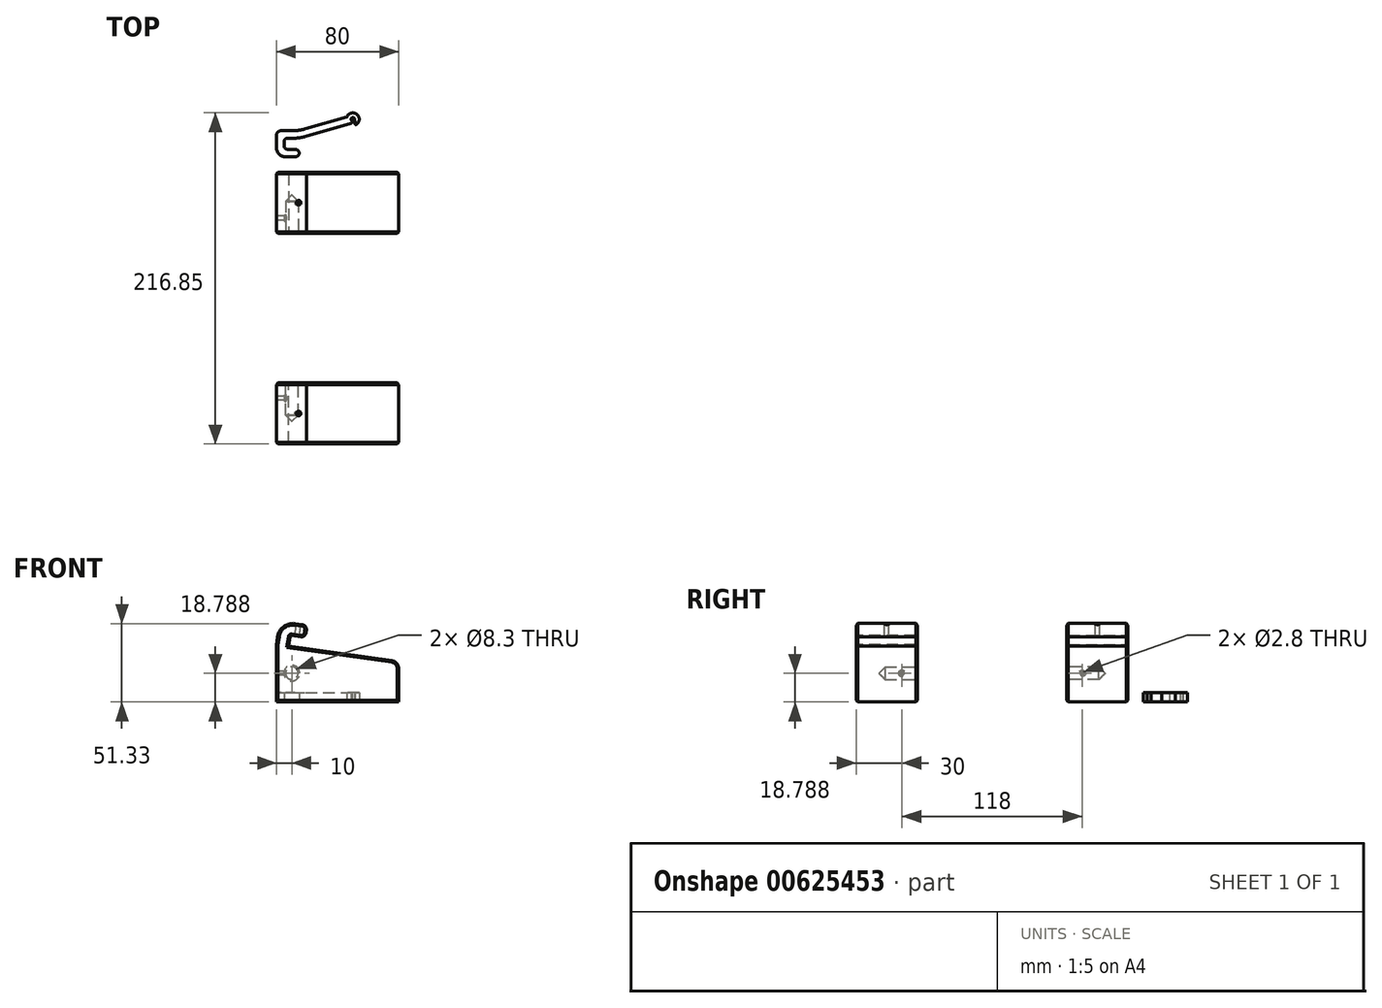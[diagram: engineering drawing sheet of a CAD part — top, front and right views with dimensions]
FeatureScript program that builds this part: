
annotation { "Feature Type Name" : "Feature", "Feature Type Description" : "" }
export const myFeature = defineFeature(function(context is Context, id is Id, definition is map)
    precondition{}
    {
        {
            var Q0;
            Q0=qCreatedBy(makeId("Front.planeOp"),FACE);
            var sketch = newSketch(context, id + "F0", { "sketchPlane" : qUnion([Q0])});
            skLineSegment(sketch, "E0", {"start": v(0, 0) * mm, "end": v(267.37, 0) * mm});
            skLineSegment(sketch, "E1", {"start": v(267.37, 0) * mm, "end": v(0, 37.58) * mm});
            skLineSegment(sketch, "E2", {"start": v(0, 37.58) * mm, "end": v(0, 0) * mm});
            skLineSegment(sketch, "E3", {"start": v(80, 26.33) * mm, "end": v(80, 0) * mm});
            skSolve(sketch);
        }
        {
            var Q0;
            {var subQ0=sQuery(id+"F0.wireOp",EDGE,"E2");Q0=makeQuery(id+"F0.imprint","IMPRINT",FACE,{"disambiguationData":[TD([[makeQuery(id+"F0.imprint","IMPRINT",EDGE,{"derivedFrom":subQ0}),1.0]])]});}
            extrude(context, id + "F1", {"entities" : qUnion([Q0]), "depth" : 40 * mm, "offsetDistance" : 25 * mm});
        }
        {
            var Q0;
            Q0=makeQuery(id+"F1.opExtrude","CAP_FACE",FACE,{"disambiguationData":[OSD([sQuery(id+"F0.wireOp",EDGE,"E0"),sQuery(id+"F0.wireOp",EDGE,"E1"),sQuery(id+"F0.wireOp",EDGE,"E2"),sQuery(id+"F0.wireOp",EDGE,"E3")])],"isStart":false});
            var sketch = newSketch(context, id + "F2", { "sketchPlane" : qUnion([Q0])});
            skCircle(sketch, "E4", {"center": v(10, 18.79) * mm, "radius": 4.15 * mm});
            skPoint(sketch, "E4.centerSnap0", {"position": v(0, 18.79) * mm});
            skSolve(sketch);
        }
        {
            var Q0;
            Q0=makeQuery(id+"F2.imprint","IMPRINT",FACE,{"disambiguationData":[TD([[makeQuery(id+"F2.imprint","IMPRINT",EDGE,{"derivedFrom":sQuery(id+"F2.wireOp",EDGE,"E4")}),1.0]])]});
            extrude(context, id + "F3", {"entities" : qUnion([Q0]), "operationType" : NewBodyOperationType.REMOVE, "oppositeDirection" : true, "depth" : 25 * mm, "offsetDistance" : 25 * mm});
        }
        {
            var Q0;
            Q0=makeQuery(id+"F3.boolean.opBoolean","COPY",EDGE,{"derivedFrom":makeQuery(id+"F3.opExtrude","CAP_EDGE",EDGE,{"disambiguationData":[OSD([sQuery(id+"F2.wireOp",EDGE,"E4")])],"isStart":false})});
            chamfer(context, id + "F4", {"entities" : qUnion([Q0]), "width" : 4 * mm, "tangentPropagation" : true});
        }
        {
            var Q0;
            Q0=makeQuery(id+"F1.opExtrude","SWEPT_FACE",FACE,{"disambiguationData":[OSD([sQuery(id+"F0.wireOp",EDGE,"E2")])]});
            var sketch = newSketch(context, id + "F5", { "sketchPlane" : qUnion([Q0])});
            skCircle(sketch, "E5", {"center": v(30, 18.79) * mm, "radius": 1.4 * mm});
            skPoint(sketch, "E5.centerSnap0", {"position": v(40, 18.79) * mm});
            skSolve(sketch);
        }
        {
            var Q0;
            Q0=makeQuery(id+"F5.imprint","IMPRINT",FACE,{"disambiguationData":[TD([[makeQuery(id+"F5.imprint","IMPRINT",EDGE,{"derivedFrom":sQuery(id+"F5.wireOp",EDGE,"E5")}),1.0]])]});
            extrude(context, id + "F6", {"entities" : qUnion([Q0]), "operationType" : NewBodyOperationType.REMOVE, "oppositeDirection" : true, "depth" : 10 * mm, "offsetDistance" : 25 * mm});
        }
        {
            var Q0;
            Q0=makeQuery(id+"F1.opExtrude","CAP_FACE",FACE,{"disambiguationData":[OSD([sQuery(id+"F0.wireOp",EDGE,"E0"),sQuery(id+"F0.wireOp",EDGE,"E1"),sQuery(id+"F0.wireOp",EDGE,"E2"),sQuery(id+"F0.wireOp",EDGE,"E3")])],"isStart":false});
            var sketch = newSketch(context, id + "F7", { "sketchPlane" : qUnion([Q0])});
            skLineSegment(sketch, "E6", {"start": v(0, 37.58) * mm, "end": v(0.72, 42.73) * mm});
            skLineSegment(sketch, "E7", {"start": v(12.02, 51.24) * mm, "end": v(19.94, 50.12) * mm});
            skLineSegment(sketch, "E8", {"start": v(19.94, 50.12) * mm, "end": v(18.83, 42.2) * mm});
            skLineSegment(sketch, "E9", {"start": v(18.83, 42.2) * mm, "end": v(8.92, 43.6) * mm});
            skLineSegment(sketch, "E10", {"start": v(8.92, 43.6) * mm, "end": v(7.92, 36.46) * mm});
            skPoint(sketch, "E11.visualSharp", {"position": v(2.12, 52.63) * mm});
            skArc(sketch, "E11.filletArc", {"start": v(12.02, 51.24) * mm, "mid": v(4.6, 49.32) * mm, "end": v(0.72, 42.73) * mm});
            skSolve(sketch);
        }
        {
            var Q0;
            {var subQ0=sQuery(id+"F7.wireOp",EDGE,"E6");Q0=makeQuery(id+"F7.imprint","IMPRINT",FACE,{"disambiguationData":[TD([[makeQuery(id+"F7.imprint","IMPRINT",EDGE,{"derivedFrom":subQ0}),-1.0]])]});}
            var Q1;
            Q1=makeQuery(id+"F1.opExtrude","CAP_FACE",FACE,{"disambiguationData":[OSD([sQuery(id+"F0.wireOp",EDGE,"E0"),sQuery(id+"F0.wireOp",EDGE,"E1"),sQuery(id+"F0.wireOp",EDGE,"E2"),sQuery(id+"F0.wireOp",EDGE,"E3")])],"isStart":true});
            extrude(context, id + "F8", {"entities" : qUnion([Q0]), "operationType" : NewBodyOperationType.ADD, "endBound" : BoundingType.UP_TO_SURFACE, "oppositeDirection" : true, "depth" : 25 * mm, "endBoundEntityFace" : qUnion([Q1]), "offsetDistance" : 25 * mm});
        }
        {
            var Q0;
            Q0=makeQuery(id+"F8.opExtrude","SWEPT_EDGE",EDGE,{"disambiguationData":[OSD([sQuery(id+"F7.wireOp",EDGE,"E9"),sQuery(id+"F7.wireOp",EDGE,"E10")])]});
            var Q1;
            Q1=makeQuery(id+"F8.opExtrude","SWEPT_EDGE",EDGE,{"disambiguationData":[OSD([sQuery(id+"F0.wireOp",EDGE,"E1"),sQuery(id+"F7.wireOp",EDGE,"E10")])]});
            fillet(context, id + "F9", {"entities" : qUnion([Q0, Q1]), "radius" : 1 * mm, "tangentPropagation" : true, "allowEdgeOverflow" : false});
        }
        {
            var Q0;
            Q0=makeQuery(id+"F8.opExtrude","SWEPT_EDGE",EDGE,{"disambiguationData":[OSD([sQuery(id+"F7.wireOp",EDGE,"E7"),sQuery(id+"F7.wireOp",EDGE,"E8")])]});
            var Q1;
            Q1=makeQuery(id+"F8.opExtrude","SWEPT_EDGE",EDGE,{"disambiguationData":[OSD([sQuery(id+"F7.wireOp",EDGE,"E8"),sQuery(id+"F7.wireOp",EDGE,"E9")])]});
            fillet(context, id + "F10", {"entities" : qUnion([Q0, Q1]), "radius" : 3 * mm, "tangentPropagation" : true, "allowEdgeOverflow" : false});
        }
        {
            var Q0;
            Q0=makeQuery(id+"F1.opExtrude","SWEPT_EDGE",EDGE,{"disambiguationData":[OSD([sQuery(id+"F0.wireOp",EDGE,"E1"),sQuery(id+"F0.wireOp",EDGE,"E3")])]});
            fillet(context, id + "F11", {"entities" : qUnion([Q0]), "radius" : 5 * mm, "tangentPropagation" : true, "allowEdgeOverflow" : false});
        }
        {
            var Q0;
            Q0=makeQuery(id+"F3.boolean.opBoolean","COPY",EDGE,{"derivedFrom":makeQuery(id+"F3.opExtrude","CAP_EDGE",EDGE,{"disambiguationData":[OSD([sQuery(id+"F2.wireOp",EDGE,"E4")])],"isStart":true})});
            var Q1;
            Q1=makeQuery(id+"F6.boolean.opBoolean","COPY",EDGE,{"derivedFrom":makeQuery(id+"F6.opExtrude","CAP_EDGE",EDGE,{"disambiguationData":[OSD([sQuery(id+"F5.wireOp",EDGE,"E5")])],"isStart":true})});
            var Q2;
            Q2=makeQuery(id+"F6.boolean.opBoolean","INTERSECT",EDGE,{"derivedFrom":[makeQuery(id+"F3.boolean.opBoolean","COPY",FACE,{"derivedFrom":makeQuery(id+"F3.opExtrude","SWEPT_FACE",FACE,{"disambiguationData":[OSD([sQuery(id+"F2.wireOp",EDGE,"E4")])]})}),makeQuery(id+"F6.opExtrude","SWEPT_FACE",FACE,{"disambiguationData":[OSD([sQuery(id+"F5.wireOp",EDGE,"E5")])]})]});
            chamfer(context, id + "F12", {"entities" : qUnion([Q0, Q1, Q2]), "width" : 1 * mm, "tangentPropagation" : true});
        }
        {
            var Q0;
            {var subQ0=sQuery(id+"F0.wireOp",EDGE,"E1");Q0=makeQuery(id+"F8.boolean.opBoolean","MERGE",FACE,{"derivedFrom":[makeQuery(id+"F1.opExtrude","CAP_FACE",FACE,{"disambiguationData":[OSD([sQuery(id+"F0.wireOp",EDGE,"E0"),subQ0,sQuery(id+"F0.wireOp",EDGE,"E2"),sQuery(id+"F0.wireOp",EDGE,"E3")])],"isStart":false}),makeQuery(id+"F8.opExtrude","CAP_FACE",FACE,{"disambiguationData":[OSD([subQ0,sQuery(id+"F7.wireOp",EDGE,"E6"),sQuery(id+"F7.wireOp",EDGE,"E7"),sQuery(id+"F7.wireOp",EDGE,"E8"),sQuery(id+"F7.wireOp",EDGE,"E9"),sQuery(id+"F7.wireOp",EDGE,"E10"),sQuery(id+"F7.wireOp",EDGE,"E11.filletArc")])],"isStart":true})]});}
            var Q1;
            {var subQ0=sQuery(id+"F0.wireOp",EDGE,"E3");var subQ1=sQuery(id+"F0.wireOp",EDGE,"E2");var subQ2=sQuery(id+"F0.wireOp",EDGE,"E1");var subQ3=sQuery(id+"F0.wireOp",EDGE,"E0");Q1=makeQuery(id+"F8.boolean.opBoolean","MERGE",FACE,{"derivedFrom":[makeQuery(id+"F1.opExtrude","CAP_FACE",FACE,{"disambiguationData":[OSD([subQ3,subQ2,subQ1,subQ0])],"isStart":true}),makeQuery(id+"F8.opExtrude","CAP_FACE",FACE,{"disambiguationData":[OSD([subQ3,subQ2,subQ1,subQ0])],"isStart":false})]});}
            chamfer(context, id + "F13", {"entities" : qUnion([Q0, Q1]), "width" : 1 * mm, "tangentPropagation" : true});
        }
        {
            var Q0;
            Q0=makeQuery(id+"F8.opExtrude","SWEPT_FACE",FACE,{"disambiguationData":[OSD([sQuery(id+"F7.wireOp",EDGE,"E7")])]});
            var sketch = newSketch(context, id + "F14", { "sketchPlane" : qUnion([Q0])});
            skCircle(sketch, "E12", {"center": v(7.27, -20) * mm, "radius": 1.5 * mm});
            skPoint(sketch, "E12.centerSnap0", {"position": v(7.27, -39) * mm});
            skPoint(sketch, "E12.centerSnap1", {"position": v(9.77, -20) * mm});
            skSolve(sketch);
        }
        {
            var Q0;
            Q0=makeQuery(id+"F14.imprint","IMPRINT",FACE,{"disambiguationData":[TD([[makeQuery(id+"F14.imprint","IMPRINT",EDGE,{"derivedFrom":sQuery(id+"F14.wireOp",EDGE,"E12")}),1.0]])]});
            extrude(context, id + "F15", {"entities" : qUnion([Q0]), "operationType" : NewBodyOperationType.REMOVE, "oppositeDirection" : true, "depth" : 10 * mm, "offsetDistance" : 25 * mm});
        }
        {
            var Q0;
            Q0=makeQuery(id+"F1.opExtrude","SWEPT_BODY",BODY,{"disambiguationData":[OSD([sQuery(id+"F0.wireOp",EDGE,"E0"),sQuery(id+"F0.wireOp",EDGE,"E1"),sQuery(id+"F0.wireOp",EDGE,"E2"),sQuery(id+"F0.wireOp",EDGE,"E3")])]});
            var Q1;
            Q1=qCreatedBy(makeId("Top.planeOp"),FACE);
            mirror(context, id + "F16", {"entities" : qUnion([Q0]), "mirrorPlane" : qUnion([Q1])});
        }
        {
            var Q0;
            Q0=makeQuery(id+"F16.opPattern","COPY",BODY,{"derivedFrom":makeQuery(id+"F1.opExtrude","SWEPT_BODY",BODY,{"disambiguationData":[OSD([sQuery(id+"F0.wireOp",EDGE,"E0"),sQuery(id+"F0.wireOp",EDGE,"E1"),sQuery(id+"F0.wireOp",EDGE,"E2"),sQuery(id+"F0.wireOp",EDGE,"E3")])]}),"instanceName":"1"});
            transform(context, id + "F17", {"entities" : qUnion([Q0]), "transformType" : TransformType.TRANSLATION_3D, "dx" : 0 * mm, "dy" : 0 * mm, "dz" : -2 * mm, "makeCopy" : false});
        }
        {
            var Q0;
            Q0=makeQuery(id+"F16.opPattern","COPY",BODY,{"derivedFrom":makeQuery(id+"F1.opExtrude","SWEPT_BODY",BODY,{"disambiguationData":[OSD([sQuery(id+"F0.wireOp",EDGE,"E0"),sQuery(id+"F0.wireOp",EDGE,"E1"),sQuery(id+"F0.wireOp",EDGE,"E2"),sQuery(id+"F0.wireOp",EDGE,"E3")])]}),"instanceName":"1"});
            var Q1;
            {var subQ0=sQuery(id+"F0.wireOp",EDGE,"E0");Q1=makeQuery(id+"F13.opChamfer","BLEND_EDGE",EDGE,{"blendedFrom":[makeQuery(id+"F1.opExtrude","CAP_EDGE",EDGE,{"disambiguationData":[OSD([subQ0])],"isStart":false}),makeQuery(id+"F1.opExtrude","SWEPT_FACE",FACE,{"disambiguationData":[OSD([subQ0])]})],"blendedInto":[makeQuery(id+"F1.opExtrude","SWEPT_FACE",FACE,{"disambiguationData":[OSD([subQ0])]})]});}
            transform(context, id + "F18", {"entities" : qUnion([Q0]), "transformType" : TransformType.ROTATION, "transformAxis" : qUnion([Q1]), "angle" : 180 * degree, "makeCopy" : false});
        }
        {
            var Q0;
            Q0=makeQuery(id+"F16.opPattern","COPY",BODY,{"derivedFrom":makeQuery(id+"F1.opExtrude","SWEPT_BODY",BODY,{"disambiguationData":[OSD([sQuery(id+"F0.wireOp",EDGE,"E0"),sQuery(id+"F0.wireOp",EDGE,"E1"),sQuery(id+"F0.wireOp",EDGE,"E2"),sQuery(id+"F0.wireOp",EDGE,"E3")])]}),"instanceName":"1"});
            transform(context, id + "F19", {"entities" : qUnion([Q0]), "transformType" : TransformType.TRANSLATION_3D, "dx" : 0 * mm, "dy" : -100 * mm, "dz" : -2 * mm, "makeCopy" : false});
        }
        {
            var Q0;
            Q0=qCreatedBy(makeId("Top.planeOp"),FACE);
            var sketch = newSketch(context, id + "F20", { "sketchPlane" : qUnion([Q0])});
            skLineSegment(sketch, "E13", {"start": v(0, 10) * mm, "end": v(0, 27.2) * mm});
            skLineSegment(sketch, "E14", {"start": v(0, 27.2) * mm, "end": v(15, 27.2) * mm});
            skLineSegment(sketch, "E15", {"start": v(50, 22.2) * mm, "end": v(5, 22.2) * mm});
            skLineSegment(sketch, "E16", {"start": v(5, 22.2) * mm, "end": v(5, 15) * mm});
            skLineSegment(sketch, "E17", {"start": v(5, 15) * mm, "end": v(15, 15) * mm});
            skLineSegment(sketch, "E18", {"start": v(15, 15) * mm, "end": v(15, 10) * mm});
            skLineSegment(sketch, "E19", {"start": v(15, 10) * mm, "end": v(0, 10) * mm});
            skPoint(sketch, "E20", {"position": v(50, 34.7) * mm});
            skCircle(sketch, "E21", {"center": v(50, 34.7) * mm, "radius": 1.15 * mm});
            skLineSegment(sketch, "E22", {"start": v(15, 22.2) * mm, "end": v(15, 27.2) * mm});
            skCircle(sketch, "E23", {"center": v(50, 34.7) * mm, "radius": 2.5 * mm});
            skLineSegment(sketch, "E24", {"start": v(49.3, 33.78) * mm, "end": v(49.7, 32.22) * mm});
            skLineSegment(sketch, "E25", {"start": v(49.3, 33.78) * mm, "end": v(51.05, 34.23) * mm});
            skLineSegment(sketch, "E26", {"start": v(51.05, 34.23) * mm, "end": v(51.45, 32.66) * mm});
            skLineSegment(sketch, "E27", {"start": v(15, 22.2) * mm, "end": v(49.7, 32.22) * mm});
            skLineSegment(sketch, "E28", {"start": v(15, 27.2) * mm, "end": v(49.3, 37.1) * mm});
            skCircle(sketch, "E29", {"center": v(50, 34.7) * mm, "radius": 4.15 * mm});
            skLineSegment(sketch, "E30", {"start": v(51.45, 32.66) * mm, "end": v(51.29, 30.76) * mm});
            skSolve(sketch);
        }
        {
            var Q0;
            Q0=makeQuery(id+"F20.imprint","IMPRINT",FACE,{"disambiguationData":[TD([[makeQuery(id+"F20.imprint","IMPRINT",EDGE,{"derivedFrom":sQuery(id+"F20.wireOp",EDGE,"E13")}),-1.0]])]});
            var Q1;
            Q1=makeQuery(id+"F20.imprint","IMPRINT",FACE,{"disambiguationData":[TD([[makeQuery(id+"F20.imprint","IMPRINT",EDGE,{"derivedFrom":sQuery(id+"F20.wireOp",EDGE,"E22")}),-1.0]])]});
            var Q2;
            {var subQ3=sQuery(id+"F20.wireOp",EDGE,"E24");Q2=makeQuery(id+"F20.imprint","IMPRINT",FACE,{"disambiguationData":[TD([[makeQuery(id+"F20.imprint","IMPRINT",EDGE,{"derivedFrom":subQ3}),-1.0]])]});}
            var Q3;
            {var subQ1=sQuery(id+"F20.wireOp",EDGE,"E23");var subQ3=sQuery(id+"F20.wireOp",EDGE,"E28");var subQ4=makeQuery(id+"F20.imprint","INTERSECT",VERTEX,{"derivedFrom":[subQ1,subQ3]});Q3=makeQuery(id+"F20.imprint","IMPRINT",FACE,{"disambiguationData":[TD([[makeQuery(id+"F20.imprint","IMPRINT",EDGE,{"disambiguationData":[TD([[subQ4,1.0]])],"derivedFrom":subQ3}),-1.0]])]});}
            var Q4;
            {var subQ1=sQuery(id+"F20.wireOp",EDGE,"E23");var subQ8=makeQuery(id+"F20.imprint","INTERSECT",VERTEX,{"derivedFrom":[subQ1,sQuery(id+"F20.wireOp",EDGE,"E26")]});Q4=makeQuery(id+"F20.imprint","IMPRINT",FACE,{"disambiguationData":[TD([[makeQuery(id+"F20.imprint","IMPRINT",EDGE,{"disambiguationData":[TD([[subQ8,-1.0]])],"derivedFrom":subQ1}),-1.0]])]});}
            extrude(context, id + "F21", {"entities" : qUnion([Q0, Q1, Q2, Q3, Q4]), "depth" : 6 * mm, "offsetDistance" : 25 * mm});
        }
        {
            var Q0;
            Q0=makeQuery(id+"F21.opExtrude","SWEPT_EDGE",EDGE,{"disambiguationData":[OSD([sQuery(id+"F20.wireOp",EDGE,"E16"),sQuery(id+"F20.wireOp",EDGE,"E17")])]});
            var Q1;
            Q1=makeQuery(id+"F21.opExtrude","SWEPT_EDGE",EDGE,{"disambiguationData":[OSD([sQuery(id+"F20.wireOp",EDGE,"E15"),sQuery(id+"F20.wireOp",EDGE,"E16")])]});
            fillet(context, id + "F22", {"entities" : qUnion([Q0, Q1]), "radius" : 2 * mm, "tangentPropagation" : true, "allowEdgeOverflow" : false});
        }
        {
            var Q0;
            Q0=makeQuery(id+"F21.opExtrude","SWEPT_EDGE",EDGE,{"disambiguationData":[OSD([sQuery(id+"F20.wireOp",EDGE,"E17"),sQuery(id+"F20.wireOp",EDGE,"E18")])]});
            var Q1;
            Q1=makeQuery(id+"F21.opExtrude","SWEPT_EDGE",EDGE,{"disambiguationData":[OSD([sQuery(id+"F20.wireOp",EDGE,"E18"),sQuery(id+"F20.wireOp",EDGE,"E19")])]});
            var Q2;
            Q2=makeQuery(id+"F21.opExtrude","SWEPT_EDGE",EDGE,{"disambiguationData":[OSD([sQuery(id+"F20.wireOp",EDGE,"E14"),sQuery(id+"F20.wireOp",EDGE,"1yIS3Pmy-LfiJ-1xFZ-S5RH-yLwdn8sh1kng")])]});
            var Q3;
            Q3=makeQuery(id+"F21.opExtrude","SWEPT_EDGE",EDGE,{"disambiguationData":[OSD([sQuery(id+"F20.wireOp",EDGE,"1yIS3Pmy-LfiJ-1xFZ-S5RH-yLwdn8sh1kng"),sQuery(id+"F20.wireOp",EDGE,"XR6DbFyx-l4WN-efZy-Vrzi-RNmAAhyDzetU")])]});
            fillet(context, id + "F23", {"entities" : qUnion([Q0, Q1, Q2, Q3]), "radius" : 3 * mm, "tangentPropagation" : true, "allowEdgeOverflow" : false});
        }
        {
            var Q0;
            Q0=makeQuery(id+"F21.opExtrude","SWEPT_EDGE",EDGE,{"disambiguationData":[OSD([sQuery(id+"F20.wireOp",EDGE,"E13"),sQuery(id+"F20.wireOp",EDGE,"E14")])]});
            var Q1;
            Q1=makeQuery(id+"F21.opExtrude","SWEPT_EDGE",EDGE,{"disambiguationData":[OSD([sQuery(id+"F20.wireOp",EDGE,"E13"),sQuery(id+"F20.wireOp",EDGE,"E19")])]});
            fillet(context, id + "F24", {"entities" : qUnion([Q0, Q1]), "radius" : 6 * mm, "tangentPropagation" : true, "allowEdgeOverflow" : false});
        }
        {
            var Q0;
            Q0=makeQuery(id+"F21.opExtrude","SWEPT_EDGE",EDGE,{"disambiguationData":[OSD([sQuery(id+"F20.wireOp",EDGE,"E15"),sQuery(id+"F20.wireOp",EDGE,"E22"),sQuery(id+"F20.wireOp",EDGE,"E27")])]});
            var Q1;
            Q1=makeQuery(id+"F21.opExtrude","SWEPT_EDGE",EDGE,{"disambiguationData":[OSD([sQuery(id+"F20.wireOp",EDGE,"E14"),sQuery(id+"F20.wireOp",EDGE,"E22"),sQuery(id+"F20.wireOp",EDGE,"E28")])]});
            fillet(context, id + "F25", {"entities" : qUnion([Q0, Q1]), "radius" : 30 * mm, "tangentPropagation" : true, "allowEdgeOverflow" : false});
        }
        {
            var Q0;
            Q0=makeQuery(id+"F21.opExtrude","SWEPT_EDGE",EDGE,{"disambiguationData":[OSD([sQuery(id+"F20.wireOp",EDGE,"E23"),sQuery(id+"F20.wireOp",EDGE,"E24"),sQuery(id+"F20.wireOp",EDGE,"E27")])]});
            chamfer(context, id + "F26", {"entities" : qUnion([Q0]), "width" : 0.8 * mm, "tangentPropagation" : true});
        }
        {
            var Q0;
            {var subQ0=sQuery(id+"F20.wireOp",EDGE,"E27");Q0=makeQuery(id+"F26.opChamfer","BLEND_EDGE",EDGE,{"blendedFrom":[makeQuery(id+"F21.opExtrude","SWEPT_EDGE",EDGE,{"disambiguationData":[OSD([sQuery(id+"F20.wireOp",EDGE,"E23"),sQuery(id+"F20.wireOp",EDGE,"E24"),subQ0])]}),makeQuery(id+"F21.opExtrude","SWEPT_FACE",FACE,{"disambiguationData":[OSD([subQ0])]})],"blendedInto":[makeQuery(id+"F21.opExtrude","SWEPT_FACE",FACE,{"disambiguationData":[OSD([subQ0])]})]});}
            var Q1;
            {var subQ0=sQuery(id+"F20.wireOp",EDGE,"E24");Q1=makeQuery(id+"F26.opChamfer","BLEND_EDGE",EDGE,{"blendedFrom":[makeQuery(id+"F21.opExtrude","SWEPT_EDGE",EDGE,{"disambiguationData":[OSD([sQuery(id+"F20.wireOp",EDGE,"E23"),subQ0,sQuery(id+"F20.wireOp",EDGE,"E27")])]}),makeQuery(id+"F21.opExtrude","SWEPT_FACE",FACE,{"disambiguationData":[OSD([subQ0])]})],"blendedInto":[makeQuery(id+"F21.opExtrude","SWEPT_FACE",FACE,{"disambiguationData":[OSD([subQ0])]})]});}
            var Q2;
            Q2=makeQuery(id+"F21.opExtrude","SWEPT_EDGE",EDGE,{"disambiguationData":[OSD([sQuery(id+"F20.wireOp",EDGE,"E21"),sQuery(id+"F20.wireOp",EDGE,"E24"),sQuery(id+"F20.wireOp",EDGE,"E25")])]});
            var Q3;
            Q3=makeQuery(id+"F21.opExtrude","SWEPT_EDGE",EDGE,{"disambiguationData":[OSD([sQuery(id+"F20.wireOp",EDGE,"E23"),sQuery(id+"F20.wireOp",EDGE,"E26"),sQuery(id+"F20.wireOp",EDGE,"E30")])]});
            var Q4;
            Q4=makeQuery(id+"F21.opExtrude","SWEPT_EDGE",EDGE,{"disambiguationData":[OSD([sQuery(id+"F20.wireOp",EDGE,"E29"),sQuery(id+"F20.wireOp",EDGE,"E30")])]});
            fillet(context, id + "F27", {"entities" : qUnion([Q0, Q1, Q2, Q3, Q4]), "radius" : 0.6 * mm, "tangentPropagation" : true, "allowEdgeOverflow" : false});
        }
    });
